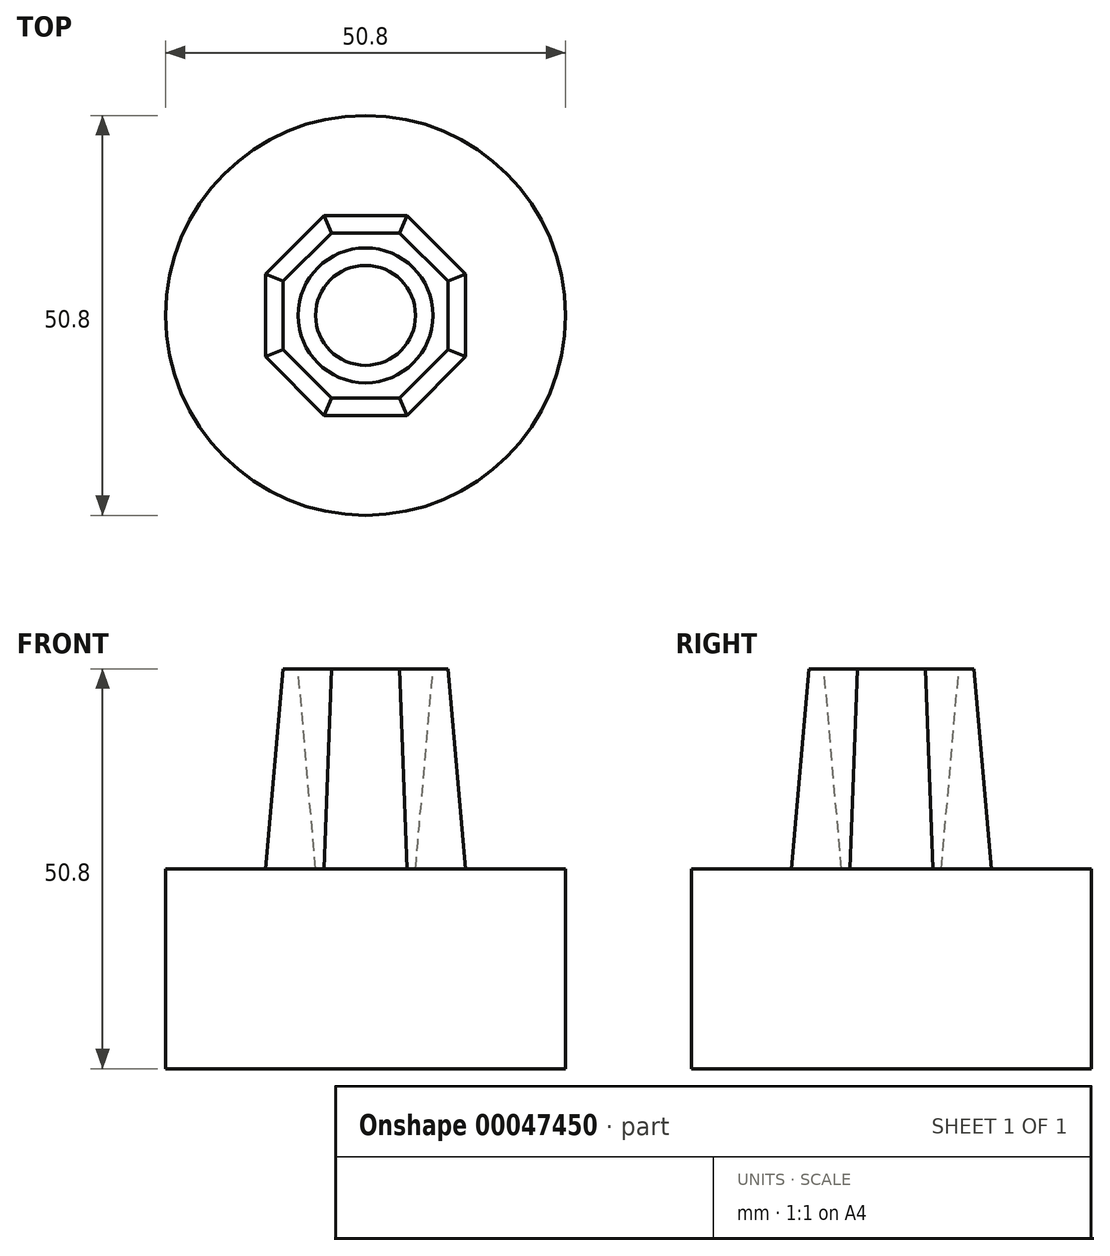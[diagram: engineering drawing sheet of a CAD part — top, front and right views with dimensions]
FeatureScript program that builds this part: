
annotation { "Feature Type Name" : "Feature", "Feature Type Description" : "" }
export const myFeature = defineFeature(function(context is Context, id is Id, definition is map)
    precondition{}
    {
        {
            var Q0;
            Q0=qCreatedBy(makeId("Top.planeOp"),FACE);
            var sketch = newSketch(context, id + "F0", { "sketchPlane" : qUnion([Q0])});
            skCircle(sketch, "E0", {"center": v(0, 0) * mm, "radius": 25.4 * mm});
            skSolve(sketch);
        }
        {
            var Q0;
            Q0=makeQuery(id+"F0.imprint","IMPRINT",FACE,{"disambiguationData":[TD([[makeQuery(id+"F0.imprint","IMPRINT",EDGE,{"derivedFrom":sQuery(id+"F0.wireOp",EDGE,"E0")}),1.0]])]});
            extrude(context, id + "F1", {"entities" : qUnion([Q0]), "endBound" : BoundingType.SYMMETRIC, "depth" : 25.4 * mm});
        }
        {
            var Q0;
            Q0=makeQuery(id+"F1.opExtrude","CAP_FACE",FACE,{"disambiguationData":[OSD([sQuery(id+"F0.wireOp",EDGE,"E0")])],"isStart":false});
            var sketch = newSketch(context, id + "F2", { "sketchPlane" : qUnion([Q0])});
            skCircle(sketch, "E1", {"center": v(0, 0) * mm, "radius": 6.35 * mm});
            skCircle(sketch, "E2.cCircle", {"center": v(0, 0) * mm, "radius": 12.7 * mm, "construction": true});
            skLineSegment(sketch, "E2.0", {"start": v(12.7, 5.26) * mm, "end": v(12.7, -5.26) * mm});
            skLineSegment(sketch, "E2.1", {"start": v(12.7, -5.26) * mm, "end": v(5.26, -12.7) * mm});
            skLineSegment(sketch, "E2.2", {"start": v(5.26, -12.7) * mm, "end": v(-5.26, -12.7) * mm});
            skLineSegment(sketch, "E2.3", {"start": v(-5.26, -12.7) * mm, "end": v(-12.7, -5.26) * mm});
            skLineSegment(sketch, "E2.4", {"start": v(-12.7, -5.26) * mm, "end": v(-12.7, 5.26) * mm});
            skLineSegment(sketch, "E2.5", {"start": v(-12.7, 5.26) * mm, "end": v(-5.26, 12.7) * mm});
            skLineSegment(sketch, "E2.6", {"start": v(-5.26, 12.7) * mm, "end": v(5.26, 12.7) * mm});
            skLineSegment(sketch, "E2.7", {"start": v(5.26, 12.7) * mm, "end": v(12.7, 5.26) * mm});
            skPoint(sketch, "E2.0.midPoint", {"position": v(12.7, 0) * mm});
            skSolve(sketch);
        }
        {
            var Q0;
            Q0=makeQuery(id+"F2.imprint","IMPRINT",FACE,{"disambiguationData":[TD([[makeQuery(id+"F2.imprint","IMPRINT",EDGE,{"derivedFrom":sQuery(id+"F2.wireOp",EDGE,"E1")}),-1.0]])]});
            extrude(context, id + "F3", {"entities" : qUnion([Q0]), "operationType" : NewBodyOperationType.ADD, "depth" : 25.4 * mm, "hasDraft" : true, "draftAngle" : 5 * degree, "draftPullDirection" : true});
        }
    });
